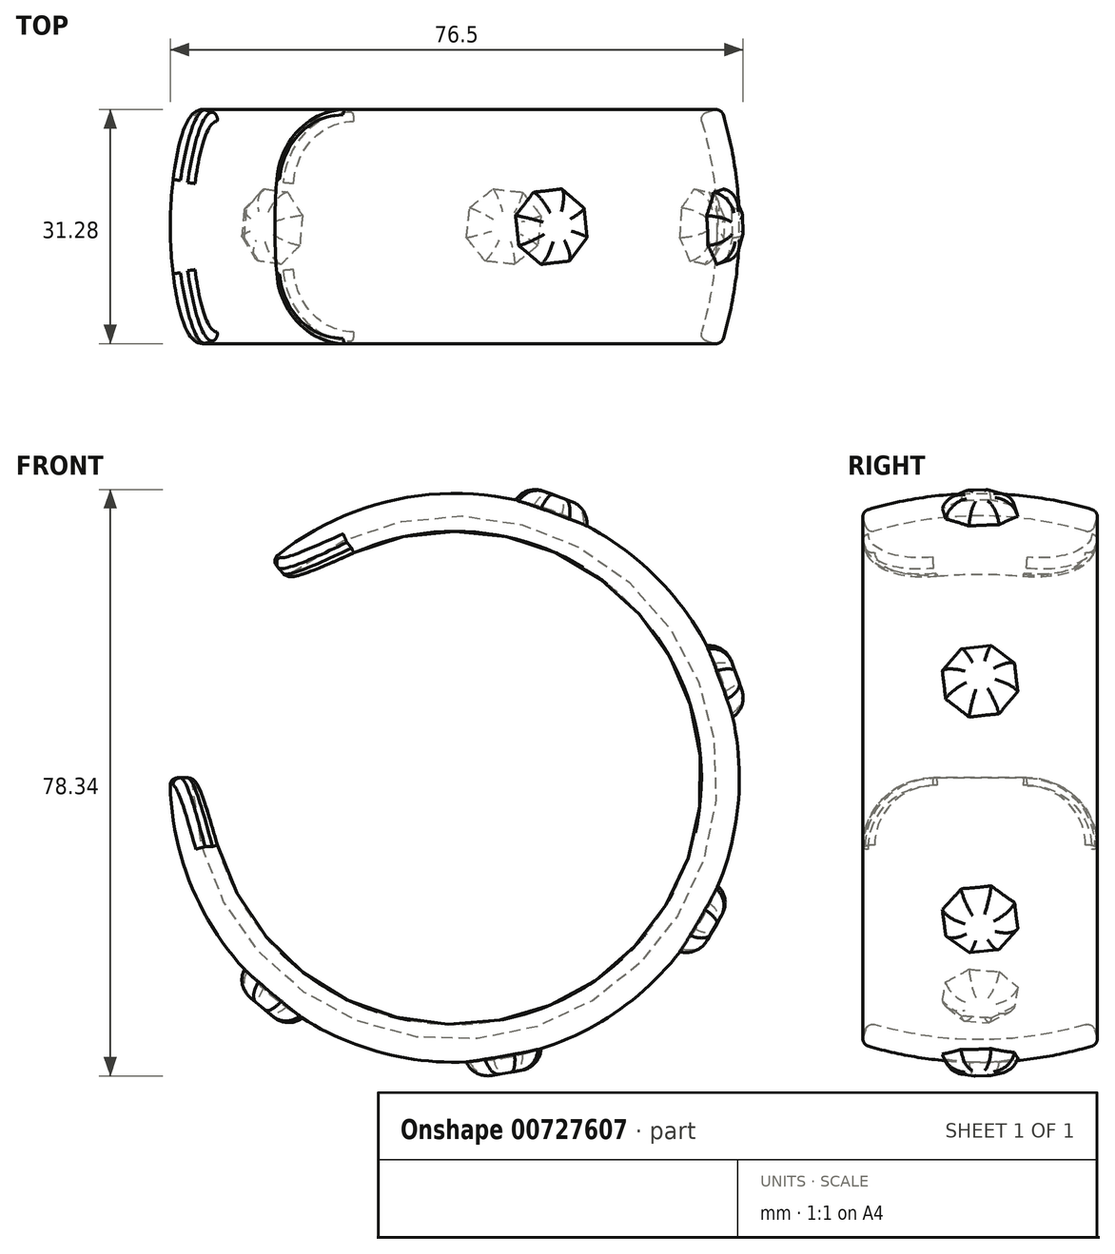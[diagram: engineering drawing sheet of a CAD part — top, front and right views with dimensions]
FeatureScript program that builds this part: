
annotation { "Feature Type Name" : "Feature", "Feature Type Description" : "" }
export const myFeature = defineFeature(function(context is Context, id is Id, definition is map)
    precondition{}
    {
        {
            var Q0;
            Q0=qCreatedBy(makeId("Top.planeOp"),FACE);
            var sketch = newSketch(context, id + "F0", { "sketchPlane" : qUnion([Q0])});
            skLineSegment(sketch, "E0", {"start": v(0, 37.97) * mm, "end": v(0, -38.43) * mm, "construction": true});
            skLineSegment(sketch, "E1", {"start": v(0, 0) * mm, "end": v(-35, 0) * mm, "construction": true});
            skArc(sketch, "E2", {"start": v(-32.7, 15) * mm, "mid": v(-35, 0) * mm, "end": v(-32.7, -15) * mm});
            skArc(sketch, "E3.0", {"start": v(-35.56, 15.9) * mm, "mid": v(-38, 0) * mm, "end": v(-35.56, -15.9) * mm});
            skLineSegment(sketch, "E4", {"start": v(-35.56, 15.9) * mm, "end": v(-32.7, 15) * mm});
            skLineSegment(sketch, "E5", {"start": v(-35.56, -15.9) * mm, "end": v(-32.7, -15) * mm});
            skSolve(sketch);
        }
        {
            var Q0;
            Q0=makeQuery(id+"F0.imprint","IMPRINT",FACE,{"disambiguationData":[TD([[makeQuery(id+"F0.imprint","IMPRINT",EDGE,{"derivedFrom":sQuery(id+"F0.wireOp",EDGE,"E2")}),-1.0]])]});
            var Q1;
            Q1=sQuery(id+"F0.wireOp",EDGE,"E0");
            revolve(context, id + "F1", {"surfaceOperationType" : NewSurfaceOperationType.NEW, "entities" : qUnion([Q0]), "axis" : qUnion([Q1]), "revolveType" : RevolveType.ONE_DIRECTION, "angle" : 310 * degree});
        }
        {
            var Q0;
            Q0=makeQuery(id+"F1.opRevolve","CAP_EDGE",EDGE,{"disambiguationData":[OSD([sQuery(id+"F0.wireOp",EDGE,"E5")])],"isStart":false});
            var Q1;
            Q1=makeQuery(id+"F1.opRevolve","CAP_EDGE",EDGE,{"disambiguationData":[OSD([sQuery(id+"F0.wireOp",EDGE,"E4")])],"isStart":false});
            var Q2;
            Q2=makeQuery(id+"F1.opRevolve","CAP_EDGE",EDGE,{"disambiguationData":[OSD([sQuery(id+"F0.wireOp",EDGE,"E4")])],"isStart":true});
            var Q3;
            Q3=makeQuery(id+"F1.opRevolve","CAP_EDGE",EDGE,{"disambiguationData":[OSD([sQuery(id+"F0.wireOp",EDGE,"E5")])],"isStart":true});
            fillet(context, id + "F2", {"entities" : qUnion([Q0, Q1, Q2, Q3]), "radius" : 10 * mm, "tangentPropagation" : true, "allowEdgeOverflow" : false});
        }
        {
            var Q0;
            Q0=makeQuery(id+"F1.opRevolve","CAP_EDGE",EDGE,{"disambiguationData":[OSD([sQuery(id+"F0.wireOp",EDGE,"E3.0")])],"isStart":false});
            var Q1;
            Q1=makeQuery(id+"F1.opRevolve","CAP_EDGE",EDGE,{"disambiguationData":[OSD([sQuery(id+"F0.wireOp",EDGE,"E2")])],"isStart":false});
            fillet(context, id + "F3", {"entities" : qUnion([Q0, Q1]), "radius" : 1 * mm, "tangentPropagation" : true, "allowEdgeOverflow" : false});
        }
        {
            var Q0;
            Q0=qCreatedBy(makeId("Front.planeOp"),FACE);
            var sketch = newSketch(context, id + "F4", { "sketchPlane" : qUnion([Q0])});
            skLineSegment(sketch, "E6", {"start": v(0, 0) * mm, "end": v(-33.45, -42.2) * mm, "construction": true});
            skLineSegment(sketch, "E7", {"start": v(0, 0) * mm, "end": v(-60.42, 0) * mm, "construction": true});
            skSolve(sketch);
        }
        {
            var Q0;
            Q0=sQuery(id+"F4.wireOp",EDGE,"E6");
            cPlane(context, id + "F5", {"entities" : qUnion([Q0]), "cplaneType" : CPlaneType.LINE_ANGLE, "offset" : 25 * mm, "angle" : 0 * degree, "width" : 150 * mm, "height" : 150 * mm});
        }
        {
            var Q0;
            Q0=qCreatedBy(id+"F5.planeOp",FACE);
            var sketch = newSketch(context, id + "F6", { "sketchPlane" : qUnion([Q0])});
            skLineSegment(sketch, "E8", {"start": v(-13.22, -39.06) * mm, "end": v(28.73, -39.06) * mm, "construction": true});
            skSolve(sketch);
        }
        {
            var Q0;
            Q0=sQuery(id+"F6.wireOp",EDGE,"E8");
            cPlane(context, id + "F7", {"entities" : qUnion([Q0]), "cplaneType" : CPlaneType.LINE_ANGLE, "offset" : 25 * mm, "angle" : 40 * degree, "oppositeDirection" : true, "width" : 150 * mm, "height" : 150 * mm});
        }
        {
            var Q0;
            Q0=qCreatedBy(id+"F7.planeOp",FACE);
            var sketch = newSketch(context, id + "F8", { "sketchPlane" : qUnion([Q0])});
            skCircle(sketch, "E9", {"center": v(0, 0) * mm, "radius": 4.5 * mm, "construction": true});
            skLineSegment(sketch, "E10.0", {"start": v(2.34, -4.27) * mm, "end": v(-1.36, -4.68) * mm});
            skLineSegment(sketch, "E10.1", {"start": v(-1.36, -4.68) * mm, "end": v(-4.27, -2.34) * mm});
            skLineSegment(sketch, "E10.2", {"start": v(-4.27, -2.34) * mm, "end": v(-4.68, 1.36) * mm});
            skLineSegment(sketch, "E10.3", {"start": v(-4.68, 1.36) * mm, "end": v(-2.34, 4.27) * mm});
            skLineSegment(sketch, "E10.4", {"start": v(-2.34, 4.27) * mm, "end": v(1.36, 4.68) * mm});
            skLineSegment(sketch, "E10.5", {"start": v(1.36, 4.68) * mm, "end": v(4.27, 2.34) * mm});
            skLineSegment(sketch, "E10.6", {"start": v(4.27, 2.34) * mm, "end": v(4.68, -1.36) * mm});
            skLineSegment(sketch, "E10.7", {"start": v(4.68, -1.36) * mm, "end": v(2.34, -4.27) * mm});
            skPoint(sketch, "E10.0.midPoint", {"position": v(0.49, -4.47) * mm});
            skSolve(sketch);
        }
        {
            var Q0;
            Q0 = qSketchRegion(id + "F8", true);
            extrude(context, id + "F9", {"entities" : qUnion([Q0]), "endBound" : BoundingType.UP_TO_NEXT, "oppositeDirection" : true, "depth" : 25 * mm, "offsetDistance" : 25 * mm, "hasDraft" : true, "draftAngle" : 15 * degree, "hasSecondDirection" : true, "secondDirectionOppositeDirection" : false, "secondDirectionDepth" : 1 * mm, "hasSecondDirectionDraft" : true, "secondDirectionDraftAngle" : 15 * degree, "secondDirectionDraftPullDirection" : true});
        }
        {
            var Q0;
            Q0=makeQuery(id+"F9.opExtrude","CAP_FACE",FACE,{"disambiguationData":[OSD([sQuery(id+"F8.wireOp",EDGE,"E10.0"),sQuery(id+"F8.wireOp",EDGE,"E10.1"),sQuery(id+"F8.wireOp",EDGE,"E10.2"),sQuery(id+"F8.wireOp",EDGE,"E10.3"),sQuery(id+"F8.wireOp",EDGE,"E10.4"),sQuery(id+"F8.wireOp",EDGE,"E10.5"),sQuery(id+"F8.wireOp",EDGE,"E10.6"),sQuery(id+"F8.wireOp",EDGE,"E10.7")])],"isStart":true});
            fillet(context, id + "F10", {"entities" : qUnion([Q0]), "radius" : 3 * mm, "tangentPropagation" : true, "allowEdgeOverflow" : false});
        }
        {
            var Q0;
            Q0=qCreatedBy(makeId("Right.planeOp"),FACE);
            var sketch = newSketch(context, id + "F11", { "sketchPlane" : qUnion([Q0])});
            skLineSegment(sketch, "E11", {"start": v(0, 0) * mm, "end": v(-109.75, 0) * mm, "construction": true});
            skSolve(sketch);
        }
        {
            var Q0;
            Q0=makeQuery(id+"F9.*.split.splitOp","SPLIT",BODY,{"derivedFrom":makeQuery(id+"F9.opExtrude","SWEPT_BODY",BODY,{"disambiguationData":[OSD([sQuery(id+"F8.wireOp",EDGE,"E10.0"),sQuery(id+"F8.wireOp",EDGE,"E10.1"),sQuery(id+"F8.wireOp",EDGE,"E10.2"),sQuery(id+"F8.wireOp",EDGE,"E10.3"),sQuery(id+"F8.wireOp",EDGE,"E10.4"),sQuery(id+"F8.wireOp",EDGE,"E10.5"),sQuery(id+"F8.wireOp",EDGE,"E10.6"),sQuery(id+"F8.wireOp",EDGE,"E10.7")])]})});
            var Q1;
            Q1=sQuery(id+"F11.wireOp",EDGE,"E11");
            circularPattern(context, id + "F12", {"entities" : qUnion([Q0]), "axis" : qUnion([Q1]), "angle" : 310 * degree, "instanceCount" : 5, "oppositeDirection" : true});
        }
    });
